# Revit family: Counter_Top-Vanity_Top-KOHLER-Marrakesh-K-14031
name_source: partatom
category: Casework
revit_build: Autodesk Revit 2015 (Build: 20140606_1530(x64)
units: mm (PartAtom-declared; Revit-internal decimal feet)

## types (1)
- 96 - Biscuit
    ADA Compliant = No
    Assembly Code = E2010
    Construction Type = Drop-in
    Date Modified = 12/03/2018
    Default Elevation = 0"
    Depth = 31"
    Description = Vanity-top with single faucet hole
    Finish = Kohler-Vitreous_China-96-Biscuit
    Hardware Included = No
    Height = 3/4"
    Manufacturer = KOHLER Co.
    MasterFormat 1995 = 08715
    MasterFormat 2004 = 08.71.73
    Material = Vitreous China
    Model = K-14031-BU-96
    Product Documentation Link = http://www.us.kohler.com
    Product Finish = Kohler-Vitreous_China-96-Biscuit
    Product Name = Marrakesh
    Product Page URL = http://www.us.kohler.com
    URL = https://www.us.kohler.com
    Width = 21 7/8"

## geometry (parser evidence)
native form markers: Sweep x6
no freeform markers — native parametric forms only
